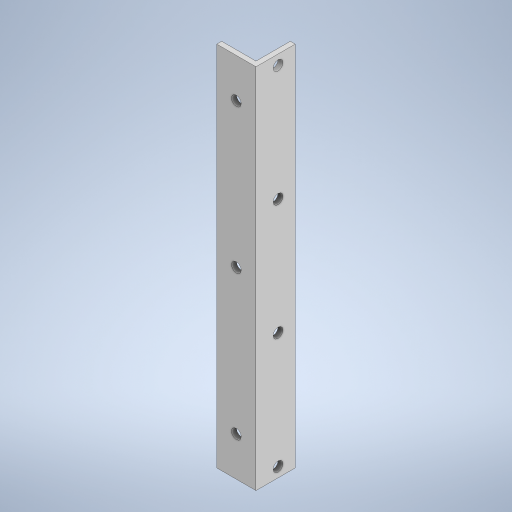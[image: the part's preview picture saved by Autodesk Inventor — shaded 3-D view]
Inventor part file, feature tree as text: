
AUTODESK INVENTOR PART (.ipt)
format: ipt  version: 2023 (Build 270158000, 158)  size: 258,560 bytes
history: native  units: in
note: dims shown in document units (in); Inventor stores cm internally (conversion verified against a paired STEP export)
features: extrude x3, sketch x3
ambient origin geometry x8: Origin, YZ Plane, XZ Plane, XY Plane, X Axis, Y Axis, Z Axis, Center Point
bodies: Solid1 (feature_tree)
feature tree (6):
  extrude  "Extrusion1"  Depth=0.125in
  extrude  "Extrusion4"  Depth=0.875in
  extrude  "Extrusion5"  Depth=9.35in
  sketch  "Sketch1"  dims[d0=1.0in d1=0.125in]
  sketch  "Sketch4"  dims[d2=0.875in d3=0.875in]
  sketch  "Sketch5"  dims[d4=9.35in d5=0.0in d23=0.25in d26=0.25in d27=0.25in d28=9.35in d29=0.0in d32=0.25in d33=0.25in d34=0.25in d35=9.35in d36=0.0in]
